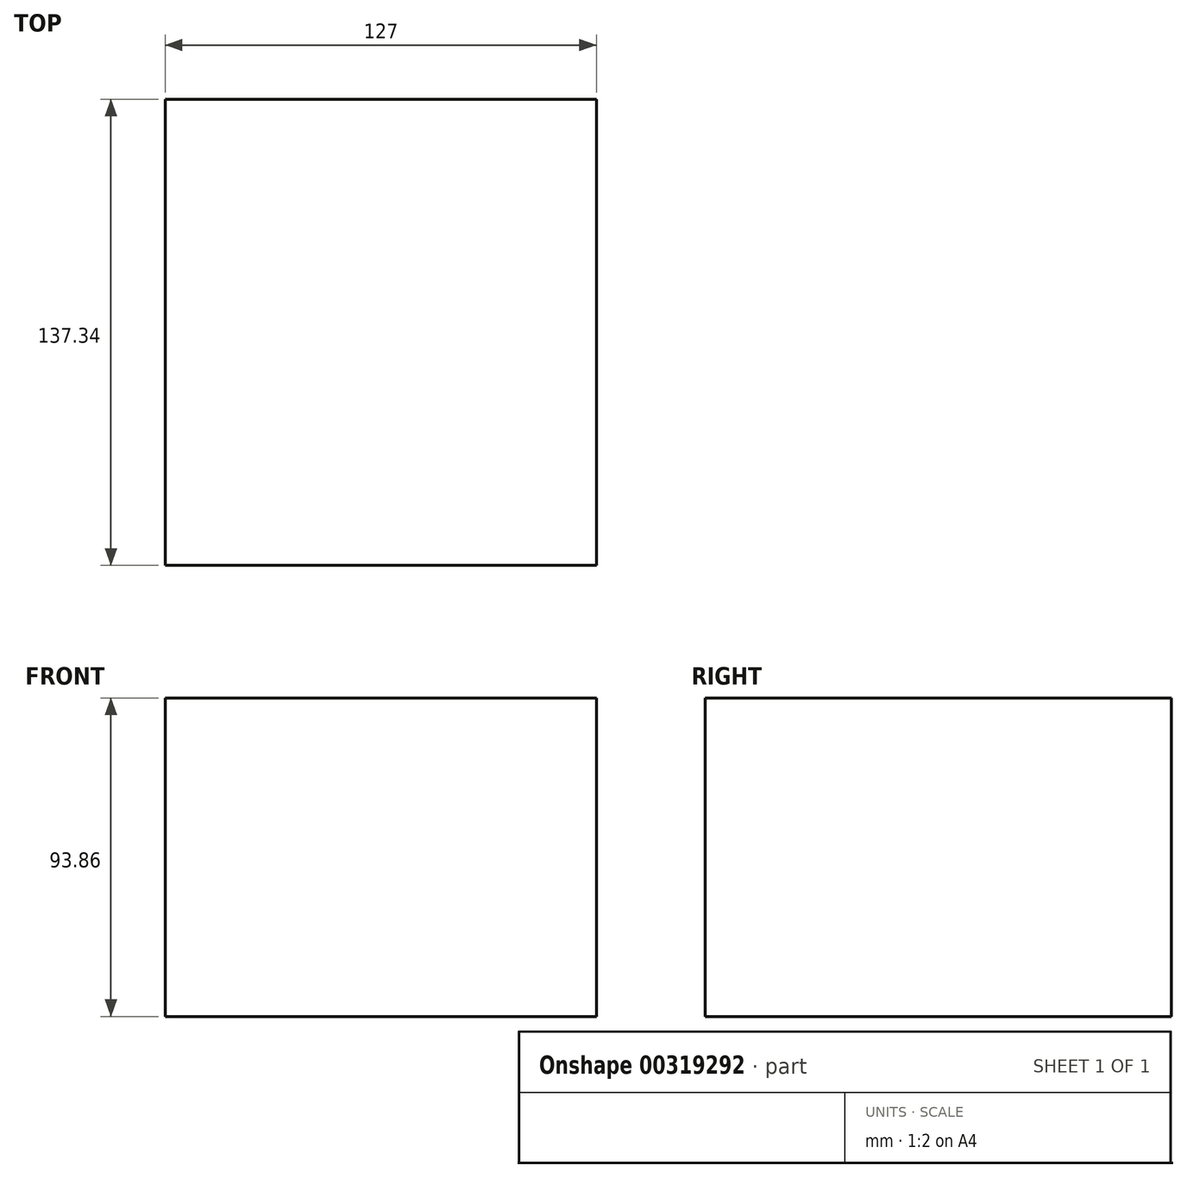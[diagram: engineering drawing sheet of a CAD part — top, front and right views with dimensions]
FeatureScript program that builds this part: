
annotation { "Feature Type Name" : "Feature", "Feature Type Description" : "" }
export const myFeature = defineFeature(function(context is Context, id is Id, definition is map)
    precondition{}
    {
        {
            var Q0;
            Q0=qCreatedBy(makeId("Right.planeOp"),FACE);
            var sketch = newSketch(context, id + "F0", { "sketchPlane" : qUnion([Q0])});
            skLineSegment(sketch, "E0.bottom", {"start": v(68.67, 34.23) * mm, "end": v(-68.67, 34.23) * mm});
            skLineSegment(sketch, "E0.top", {"start": v(68.67, -34.23) * mm, "end": v(-68.67, -34.23) * mm});
            skLineSegment(sketch, "E0.left", {"start": v(68.67, 34.23) * mm, "end": v(68.67, -34.23) * mm});
            skLineSegment(sketch, "E0.right", {"start": v(-68.67, 34.23) * mm, "end": v(-68.67, -34.23) * mm});
            skPoint(sketch, "E0.middle", {"position": v(0, 0) * mm});
            skSolve(sketch);
        }
        {
            var Q0;
            Q0=makeQuery(id+"F0.imprint","IMPRINT",FACE,{"disambiguationData":[TD([[makeQuery(id+"F0.imprint","IMPRINT",EDGE,{"derivedFrom":sQuery(id+"F0.wireOp",EDGE,"E0.bottom")}),1.0]])]});
            extrude(context, id + "F1", {"entities" : qUnion([Q0]), "endBound" : BoundingType.SYMMETRIC, "depth" : 127 * mm});
        }
        {
            var Q0;
            Q0=makeQuery(id+"F1.opExtrude","SWEPT_FACE",FACE,{"disambiguationData":[OSD([sQuery(id+"F0.wireOp",EDGE,"E0.top")])]});
            extrude(context, id + "F2", {"entities" : qUnion([Q0]), "operationType" : NewBodyOperationType.ADD, "depth" : 25.4 * mm});
        }
    });
